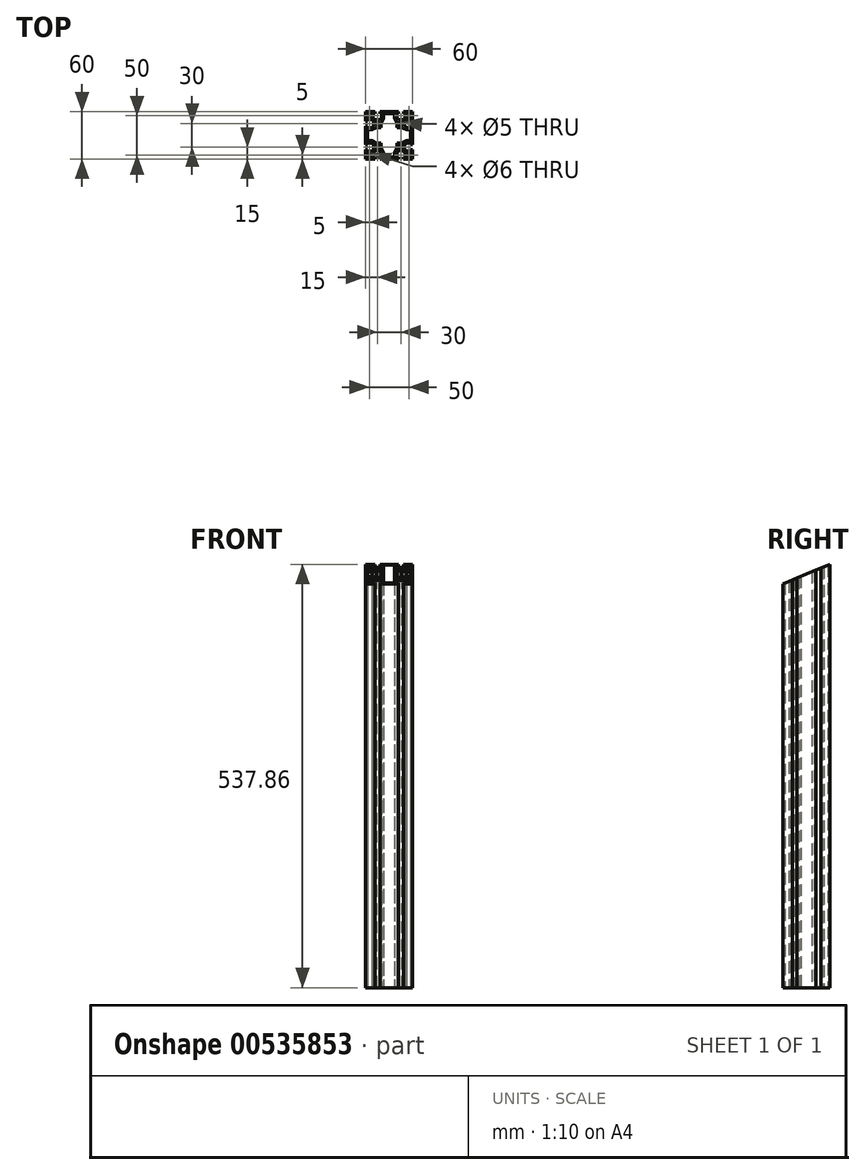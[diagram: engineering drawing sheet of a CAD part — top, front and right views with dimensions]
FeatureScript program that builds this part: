
annotation { "Feature Type Name" : "Feature", "Feature Type Description" : "" }
export const myFeature = defineFeature(function(context is Context, id is Id, definition is map)
    precondition{}
    {
        {
            var Q0;
            Q0=qCreatedBy(makeId("Top.planeOp"),FACE);
            var sketch = newSketch(context, id + "F0", { "sketchPlane" : qUnion([Q0])});
            skLineSegment(sketch, "E0.bottom", {"start": v(30, -30) * mm, "end": v(-30, -30) * mm});
            skLineSegment(sketch, "E0.top", {"start": v(30, 30) * mm, "end": v(-30, 30) * mm});
            skLineSegment(sketch, "E0.left", {"start": v(30, -30) * mm, "end": v(30, 30) * mm});
            skLineSegment(sketch, "E0.right", {"start": v(-30, -30) * mm, "end": v(-30, 30) * mm});
            skPoint(sketch, "E0.middle", {"position": v(0, 0) * mm});
            skLineSegment(sketch, "E1.top", {"start": v(-11.85, 30) * mm, "end": v(-18.15, 30) * mm});
            skLineSegment(sketch, "E1.left", {"start": v(-11.85, 27.5) * mm, "end": v(-11.85, 30) * mm});
            skLineSegment(sketch, "E1.right", {"start": v(-18.15, 27.5) * mm, "end": v(-18.15, 30) * mm});
            skPoint(sketch, "E1.middle", {"position": v(-15, 28.75) * mm});
            skLineSegment(sketch, "E2.bottom", {"start": v(-9.85, 27.5) * mm, "end": v(-11.85, 27.5) * mm});
            skLineSegment(sketch, "E2.left", {"start": v(-9.85, 27.5) * mm, "end": v(-9.85, 21.55) * mm});
            skLineSegment(sketch, "E2.right", {"start": v(-20.15, 27.5) * mm, "end": v(-20.15, 21.55) * mm});
            skPoint(sketch, "E2.middle", {"position": v(-15, 24.52) * mm});
            skArc(sketch, "E3", {"start": v(-20.15, 21.55) * mm, "mid": v(-15, 19.5) * mm, "end": v(-9.85, 21.55) * mm});
            skPoint(sketch, "E4.MirrorP", {"position": v(15, 24.52) * mm});
            skPoint(sketch, "E5.MirrorP", {"position": v(15, 28.75) * mm});
            skLineSegment(sketch, "E6.MirrorCS", {"start": v(11.85, 27.5) * mm, "end": v(11.85, 30) * mm});
            skLineSegment(sketch, "E7.MirrorCS", {"start": v(18.15, 27.5) * mm, "end": v(18.15, 30) * mm});
            skLineSegment(sketch, "E8.MirrorCS", {"start": v(9.85, 27.5) * mm, "end": v(11.85, 27.5) * mm});
            skLineSegment(sketch, "E9.MirrorCS", {"start": v(9.85, 27.5) * mm, "end": v(9.85, 21.55) * mm});
            skArc(sketch, "E10.MirrorCS", {"start": v(20.15, 21.55) * mm, "mid": v(15, 19.5) * mm, "end": v(9.85, 21.55) * mm});
            skLineSegment(sketch, "E11.MirrorCS", {"start": v(20.15, 27.5) * mm, "end": v(20.15, 21.55) * mm});
            skLineSegment(sketch, "E12.MirrorCS", {"start": v(11.85, 30) * mm, "end": v(18.15, 30) * mm});
            skLineSegment(sketch, "E13.1.0", {"start": v(27.5, 20.15) * mm, "end": v(21.55, 20.15) * mm});
            skLineSegment(sketch, "E13.1.1", {"start": v(27.5, 9.85) * mm, "end": v(21.55, 9.85) * mm});
            skArc(sketch, "E13.1.2", {"start": v(21.55, 20.15) * mm, "mid": v(19.5, 15) * mm, "end": v(21.55, 9.85) * mm});
            skLineSegment(sketch, "E13.1.3", {"start": v(27.5, -9.85) * mm, "end": v(21.55, -9.85) * mm});
            skLineSegment(sketch, "E13.1.4", {"start": v(27.5, -20.15) * mm, "end": v(21.55, -20.15) * mm});
            skPoint(sketch, "E13.1.5", {"position": v(28.75, 15) * mm});
            skPoint(sketch, "E13.1.6", {"position": v(28.75, -15) * mm});
            skArc(sketch, "E13.1.7", {"start": v(21.55, -20.15) * mm, "mid": v(19.5, -15) * mm, "end": v(21.55, -9.85) * mm});
            skPoint(sketch, "E13.1.8", {"position": v(24.52, -15) * mm});
            skPoint(sketch, "E13.1.9", {"position": v(24.52, 15) * mm});
            skLineSegment(sketch, "E13.1.10", {"start": v(27.5, 9.85) * mm, "end": v(27.5, 20.15) * mm});
            skLineSegment(sketch, "E13.1.11", {"start": v(27.5, -11.85) * mm, "end": v(27.5, -18.15) * mm});
            skLineSegment(sketch, "E13.1.12", {"start": v(30, 11.85) * mm, "end": v(30, 18.15) * mm});
            skLineSegment(sketch, "E13.1.13", {"start": v(30, -11.85) * mm, "end": v(30, -18.15) * mm});
            skLineSegment(sketch, "E13.1.14", {"start": v(27.5, 18.15) * mm, "end": v(30, 18.15) * mm});
            skLineSegment(sketch, "E13.1.15", {"start": v(27.5, 11.85) * mm, "end": v(30, 11.85) * mm});
            skLineSegment(sketch, "E13.1.16", {"start": v(27.5, 11.85) * mm, "end": v(27.5, 18.15) * mm});
            skLineSegment(sketch, "E13.1.17", {"start": v(27.5, -9.85) * mm, "end": v(27.5, -20.15) * mm});
            skLineSegment(sketch, "E13.1.18", {"start": v(27.5, -18.15) * mm, "end": v(30, -18.15) * mm});
            skLineSegment(sketch, "E13.1.19", {"start": v(27.5, -11.85) * mm, "end": v(30, -11.85) * mm});
            skLineSegment(sketch, "E13.2.0", {"start": v(20.15, -27.5) * mm, "end": v(20.15, -21.55) * mm});
            skLineSegment(sketch, "E13.2.1", {"start": v(9.85, -27.5) * mm, "end": v(9.85, -21.55) * mm});
            skArc(sketch, "E13.2.2", {"start": v(20.15, -21.55) * mm, "mid": v(15, -19.5) * mm, "end": v(9.85, -21.55) * mm});
            skLineSegment(sketch, "E13.2.3", {"start": v(-9.85, -27.5) * mm, "end": v(-9.85, -21.55) * mm});
            skLineSegment(sketch, "E13.2.4", {"start": v(-20.15, -27.5) * mm, "end": v(-20.15, -21.55) * mm});
            skPoint(sketch, "E13.2.5", {"position": v(15, -28.75) * mm});
            skPoint(sketch, "E13.2.6", {"position": v(-15, -28.75) * mm});
            skArc(sketch, "E13.2.7", {"start": v(-20.15, -21.55) * mm, "mid": v(-15, -19.5) * mm, "end": v(-9.85, -21.55) * mm});
            skPoint(sketch, "E13.2.8", {"position": v(-15, -24.52) * mm});
            skPoint(sketch, "E13.2.9", {"position": v(15, -24.52) * mm});
            skLineSegment(sketch, "E13.2.10", {"start": v(9.85, -27.5) * mm, "end": v(20.15, -27.5) * mm});
            skLineSegment(sketch, "E13.2.11", {"start": v(-11.85, -27.5) * mm, "end": v(-18.15, -27.5) * mm});
            skLineSegment(sketch, "E13.2.12", {"start": v(11.85, -30) * mm, "end": v(18.15, -30) * mm});
            skLineSegment(sketch, "E13.2.13", {"start": v(-11.85, -30) * mm, "end": v(-18.15, -30) * mm});
            skLineSegment(sketch, "E13.2.14", {"start": v(18.15, -27.5) * mm, "end": v(18.15, -30) * mm});
            skLineSegment(sketch, "E13.2.15", {"start": v(11.85, -27.5) * mm, "end": v(11.85, -30) * mm});
            skLineSegment(sketch, "E13.2.16", {"start": v(11.85, -27.5) * mm, "end": v(18.15, -27.5) * mm});
            skLineSegment(sketch, "E13.2.17", {"start": v(-9.85, -27.5) * mm, "end": v(-20.15, -27.5) * mm});
            skLineSegment(sketch, "E13.2.18", {"start": v(-18.15, -27.5) * mm, "end": v(-18.15, -30) * mm});
            skLineSegment(sketch, "E13.2.19", {"start": v(-11.85, -27.5) * mm, "end": v(-11.85, -30) * mm});
            skLineSegment(sketch, "E13.3.0", {"start": v(-27.5, -20.15) * mm, "end": v(-21.55, -20.15) * mm});
            skLineSegment(sketch, "E13.3.1", {"start": v(-27.5, -9.85) * mm, "end": v(-21.55, -9.85) * mm});
            skArc(sketch, "E13.3.2", {"start": v(-21.55, -20.15) * mm, "mid": v(-19.5, -15) * mm, "end": v(-21.55, -9.85) * mm});
            skLineSegment(sketch, "E13.3.3", {"start": v(-27.5, 9.85) * mm, "end": v(-21.55, 9.85) * mm});
            skLineSegment(sketch, "E13.3.4", {"start": v(-27.5, 20.15) * mm, "end": v(-21.55, 20.15) * mm});
            skPoint(sketch, "E13.3.5", {"position": v(-28.75, -15) * mm});
            skPoint(sketch, "E13.3.6", {"position": v(-28.75, 15) * mm});
            skArc(sketch, "E13.3.7", {"start": v(-21.55, 20.15) * mm, "mid": v(-19.5, 15) * mm, "end": v(-21.55, 9.85) * mm});
            skPoint(sketch, "E13.3.8", {"position": v(-24.52, 15) * mm});
            skPoint(sketch, "E13.3.9", {"position": v(-24.52, -15) * mm});
            skLineSegment(sketch, "E13.3.10", {"start": v(-27.5, -9.85) * mm, "end": v(-27.5, -20.15) * mm});
            skLineSegment(sketch, "E13.3.11", {"start": v(-27.5, 11.85) * mm, "end": v(-27.5, 18.15) * mm});
            skLineSegment(sketch, "E13.3.12", {"start": v(-30, -11.85) * mm, "end": v(-30, -18.15) * mm});
            skLineSegment(sketch, "E13.3.13", {"start": v(-30, 11.85) * mm, "end": v(-30, 18.15) * mm});
            skLineSegment(sketch, "E13.3.14", {"start": v(-27.5, -18.15) * mm, "end": v(-30, -18.15) * mm});
            skLineSegment(sketch, "E13.3.15", {"start": v(-27.5, -11.85) * mm, "end": v(-30, -11.85) * mm});
            skLineSegment(sketch, "E13.3.16", {"start": v(-27.5, -11.85) * mm, "end": v(-27.5, -18.15) * mm});
            skLineSegment(sketch, "E13.3.17", {"start": v(-27.5, 9.85) * mm, "end": v(-27.5, 20.15) * mm});
            skLineSegment(sketch, "E13.3.18", {"start": v(-27.5, 18.15) * mm, "end": v(-30, 18.15) * mm});
            skLineSegment(sketch, "E13.3.19", {"start": v(-27.5, 11.85) * mm, "end": v(-30, 11.85) * mm});
            skLineSegment(sketch, "E13.anchor1", {"start": v(0, 0) * mm, "end": v(-20.15, 21.55) * mm, "construction": true});
            skLineSegment(sketch, "E13.anchor2", {"start": v(0, 0) * mm, "end": v(-21.55, -20.15) * mm, "construction": true});
            skLineSegment(sketch, "E14.trimOffspring", {"start": v(-18.15, 27.5) * mm, "end": v(-20.15, 27.5) * mm});
            skLineSegment(sketch, "E15.trimOffspring", {"start": v(18.15, 27.5) * mm, "end": v(20.15, 27.5) * mm});
            skCircle(sketch, "E16", {"center": v(-15, 15) * mm, "radius": 2.5 * mm});
            skCircle(sketch, "E17", {"center": v(-25, 25) * mm, "radius": 3 * mm});
            skCircle(sketch, "E18.MirrorC", {"center": v(25, 25) * mm, "radius": 3 * mm});
            skCircle(sketch, "E19.MirrorC", {"center": v(25, -25) * mm, "radius": 3 * mm});
            skCircle(sketch, "E20.MirrorC", {"center": v(-25, -25) * mm, "radius": 3 * mm});
            skCircle(sketch, "E21.MirrorC", {"center": v(15, 15) * mm, "radius": 2.5 * mm});
            skCircle(sketch, "E22.MirrorC", {"center": v(15, -15) * mm, "radius": 2.5 * mm});
            skCircle(sketch, "E23.MirrorC", {"center": v(-15, -15) * mm, "radius": 2.5 * mm});
            skLineSegment(sketch, "E24", {"start": v(-7, 27.5) * mm, "end": v(0, 27.5) * mm});
            skLineSegment(sketch, "E25", {"start": v(-7, 27.5) * mm, "end": v(-7, 22) * mm});
            skLineSegment(sketch, "E26", {"start": v(-10, 10) * mm, "end": v(-10, 16) * mm});
            skLineSegment(sketch, "E27", {"start": v(-10, 16) * mm, "end": v(-7, 22) * mm});
            skLineSegment(sketch, "E28.MirrorCS", {"start": v(10, 10) * mm, "end": v(10, 16) * mm});
            skLineSegment(sketch, "E29.MirrorCS", {"start": v(10, 16) * mm, "end": v(7, 22) * mm});
            skLineSegment(sketch, "E30.MirrorCS", {"start": v(7, 27.5) * mm, "end": v(0, 27.5) * mm});
            skLineSegment(sketch, "E31.MirrorCS", {"start": v(7, 27.5) * mm, "end": v(7, 22) * mm});
            skLineSegment(sketch, "E32.1.0", {"start": v(-10, -10) * mm, "end": v(-16, -10) * mm});
            skLineSegment(sketch, "E32.1.1", {"start": v(-16, -10) * mm, "end": v(-22, -7) * mm});
            skLineSegment(sketch, "E32.1.2", {"start": v(-27.5, -7) * mm, "end": v(-22, -7) * mm});
            skLineSegment(sketch, "E32.1.3", {"start": v(-27.5, -7) * mm, "end": v(-27.5, 0) * mm});
            skLineSegment(sketch, "E32.1.4", {"start": v(-27.5, 7) * mm, "end": v(-27.5, 0) * mm});
            skLineSegment(sketch, "E32.1.5", {"start": v(-27.5, 7) * mm, "end": v(-22, 7) * mm});
            skLineSegment(sketch, "E32.1.6", {"start": v(-16, 10) * mm, "end": v(-22, 7) * mm});
            skLineSegment(sketch, "E32.1.7", {"start": v(-10, 10) * mm, "end": v(-16, 10) * mm});
            skLineSegment(sketch, "E32.2.0", {"start": v(10, -10) * mm, "end": v(10, -16) * mm});
            skLineSegment(sketch, "E32.2.1", {"start": v(10, -16) * mm, "end": v(7, -22) * mm});
            skLineSegment(sketch, "E32.2.2", {"start": v(7, -27.5) * mm, "end": v(7, -22) * mm});
            skLineSegment(sketch, "E32.2.3", {"start": v(7, -27.5) * mm, "end": v(0, -27.5) * mm});
            skLineSegment(sketch, "E32.2.4", {"start": v(-7, -27.5) * mm, "end": v(0, -27.5) * mm});
            skLineSegment(sketch, "E32.2.5", {"start": v(-7, -27.5) * mm, "end": v(-7, -22) * mm});
            skLineSegment(sketch, "E32.2.6", {"start": v(-10, -16) * mm, "end": v(-7, -22) * mm});
            skLineSegment(sketch, "E32.2.7", {"start": v(-10, -10) * mm, "end": v(-10, -16) * mm});
            skLineSegment(sketch, "E32.3.0", {"start": v(10, 10) * mm, "end": v(16, 10) * mm});
            skLineSegment(sketch, "E32.3.1", {"start": v(16, 10) * mm, "end": v(22, 7) * mm});
            skLineSegment(sketch, "E32.3.2", {"start": v(27.5, 7) * mm, "end": v(22, 7) * mm});
            skLineSegment(sketch, "E32.3.3", {"start": v(27.5, 7) * mm, "end": v(27.5, 0) * mm});
            skLineSegment(sketch, "E32.3.4", {"start": v(27.5, -7) * mm, "end": v(27.5, 0) * mm});
            skLineSegment(sketch, "E32.3.5", {"start": v(27.5, -7) * mm, "end": v(22, -7) * mm});
            skLineSegment(sketch, "E32.3.6", {"start": v(16, -10) * mm, "end": v(22, -7) * mm});
            skLineSegment(sketch, "E32.3.7", {"start": v(10, -10) * mm, "end": v(16, -10) * mm});
            skSolve(sketch);
        }
        {
            var Q0;
            {var subQ30=sQuery(id+"F0.wireOp",EDGE,"E1.left");Q0=makeQuery(id+"F0.imprint","IMPRINT",FACE,{"disambiguationData":[TD([[makeQuery(id+"F0.imprint","IMPRINT",EDGE,{"derivedFrom":subQ30}),-1.0]])]});}
            extrude(context, id + "F1", {"entities" : qUnion([Q0]), "depth" : 537.86 * mm, "offsetDistance" : 25 * mm});
        }
        {
            var Q0;
            Q0=makeQuery(id+"F1.opExtrude","SWEPT_EDGE",EDGE,{"disambiguationData":[OSD([sQuery(id+"F0.wireOp",EDGE,"E24"),sQuery(id+"F0.wireOp",EDGE,"E25")])]});
            var Q1;
            Q1=makeQuery(id+"F1.opExtrude","SWEPT_EDGE",EDGE,{"disambiguationData":[OSD([sQuery(id+"F0.wireOp",EDGE,"E30.MirrorCS"),sQuery(id+"F0.wireOp",EDGE,"E31.MirrorCS")])]});
            var Q2;
            Q2=makeQuery(id+"F1.opExtrude","SWEPT_EDGE",EDGE,{"disambiguationData":[OSD([sQuery(id+"F0.wireOp",EDGE,"840db5bc-c403-45cd-90c7-254e62d9e8c5.3.2"),sQuery(id+"F0.wireOp",EDGE,"840db5bc-c403-45cd-90c7-254e62d9e8c5.3.3")])]});
            var Q3;
            Q3=makeQuery(id+"F1.opExtrude","SWEPT_EDGE",EDGE,{"disambiguationData":[OSD([sQuery(id+"F0.wireOp",EDGE,"840db5bc-c403-45cd-90c7-254e62d9e8c5.3.4"),sQuery(id+"F0.wireOp",EDGE,"840db5bc-c403-45cd-90c7-254e62d9e8c5.3.5")])]});
            var Q4;
            Q4=makeQuery(id+"F1.opExtrude","SWEPT_EDGE",EDGE,{"disambiguationData":[OSD([sQuery(id+"F0.wireOp",EDGE,"840db5bc-c403-45cd-90c7-254e62d9e8c5.1.4"),sQuery(id+"F0.wireOp",EDGE,"840db5bc-c403-45cd-90c7-254e62d9e8c5.1.5")])]});
            var Q5;
            Q5=makeQuery(id+"F1.opExtrude","SWEPT_EDGE",EDGE,{"disambiguationData":[OSD([sQuery(id+"F0.wireOp",EDGE,"840db5bc-c403-45cd-90c7-254e62d9e8c5.1.2"),sQuery(id+"F0.wireOp",EDGE,"840db5bc-c403-45cd-90c7-254e62d9e8c5.1.3")])]});
            var Q6;
            Q6=makeQuery(id+"F1.opExtrude","SWEPT_EDGE",EDGE,{"disambiguationData":[OSD([sQuery(id+"F0.wireOp",EDGE,"840db5bc-c403-45cd-90c7-254e62d9e8c5.2.2"),sQuery(id+"F0.wireOp",EDGE,"840db5bc-c403-45cd-90c7-254e62d9e8c5.2.3")])]});
            var Q7;
            Q7=makeQuery(id+"F1.opExtrude","SWEPT_EDGE",EDGE,{"disambiguationData":[OSD([sQuery(id+"F0.wireOp",EDGE,"840db5bc-c403-45cd-90c7-254e62d9e8c5.2.4"),sQuery(id+"F0.wireOp",EDGE,"840db5bc-c403-45cd-90c7-254e62d9e8c5.2.5")])]});
            fillet(context, id + "F2", {"entities" : qUnion([Q0, Q1, Q2, Q3, Q4, Q5, Q6, Q7]), "radius" : 2 * mm, "tangentPropagation" : true, "allowEdgeOverflow" : false});
        }
        {
            var Q0;
            Q0=makeQuery(id+"F1.opExtrude","SWEPT_EDGE",EDGE,{"disambiguationData":[OSD([sQuery(id+"F0.wireOp",EDGE,"E26"),sQuery(id+"F0.wireOp",EDGE,"E27")])]});
            var Q1;
            Q1=makeQuery(id+"F1.opExtrude","SWEPT_EDGE",EDGE,{"disambiguationData":[OSD([sQuery(id+"F0.wireOp",EDGE,"E28.MirrorCS"),sQuery(id+"F0.wireOp",EDGE,"E29.MirrorCS")])]});
            var Q2;
            Q2=makeQuery(id+"F1.opExtrude","SWEPT_EDGE",EDGE,{"disambiguationData":[OSD([sQuery(id+"F0.wireOp",EDGE,"840db5bc-c403-45cd-90c7-254e62d9e8c5.3.0"),sQuery(id+"F0.wireOp",EDGE,"840db5bc-c403-45cd-90c7-254e62d9e8c5.3.1")])]});
            var Q3;
            Q3=makeQuery(id+"F1.opExtrude","SWEPT_EDGE",EDGE,{"disambiguationData":[OSD([sQuery(id+"F0.wireOp",EDGE,"840db5bc-c403-45cd-90c7-254e62d9e8c5.1.6"),sQuery(id+"F0.wireOp",EDGE,"840db5bc-c403-45cd-90c7-254e62d9e8c5.1.7")])]});
            var Q4;
            Q4=makeQuery(id+"F1.opExtrude","SWEPT_EDGE",EDGE,{"disambiguationData":[OSD([sQuery(id+"F0.wireOp",EDGE,"840db5bc-c403-45cd-90c7-254e62d9e8c5.1.0"),sQuery(id+"F0.wireOp",EDGE,"840db5bc-c403-45cd-90c7-254e62d9e8c5.1.1")])]});
            var Q5;
            Q5=makeQuery(id+"F1.opExtrude","SWEPT_EDGE",EDGE,{"disambiguationData":[OSD([sQuery(id+"F0.wireOp",EDGE,"840db5bc-c403-45cd-90c7-254e62d9e8c5.3.6"),sQuery(id+"F0.wireOp",EDGE,"840db5bc-c403-45cd-90c7-254e62d9e8c5.3.7")])]});
            var Q6;
            Q6=makeQuery(id+"F1.opExtrude","SWEPT_EDGE",EDGE,{"disambiguationData":[OSD([sQuery(id+"F0.wireOp",EDGE,"840db5bc-c403-45cd-90c7-254e62d9e8c5.2.0"),sQuery(id+"F0.wireOp",EDGE,"840db5bc-c403-45cd-90c7-254e62d9e8c5.2.1")])]});
            var Q7;
            Q7=makeQuery(id+"F1.opExtrude","SWEPT_EDGE",EDGE,{"disambiguationData":[OSD([sQuery(id+"F0.wireOp",EDGE,"840db5bc-c403-45cd-90c7-254e62d9e8c5.2.6"),sQuery(id+"F0.wireOp",EDGE,"840db5bc-c403-45cd-90c7-254e62d9e8c5.2.7")])]});
            fillet(context, id + "F3", {"entities" : qUnion([Q0, Q1, Q2, Q3, Q4, Q5, Q6, Q7]), "radius" : 7 * mm, "tangentPropagation" : true, "allowEdgeOverflow" : false});
        }
        {
            var Q0;
            Q0=qCreatedBy(makeId("Right.planeOp"),FACE);
            var sketch = newSketch(context, id + "F4", { "sketchPlane" : qUnion([Q0])});
            skLineSegment(sketch, "E33.bottom", {"start": v(-234.13, 733.04) * mm, "end": v(-77.69, 797.84) * mm});
            skLineSegment(sketch, "E33.top", {"start": v(-126.44, 473.06) * mm, "end": v(30, 537.86) * mm});
            skLineSegment(sketch, "E33.left", {"start": v(-234.13, 733.04) * mm, "end": v(-126.44, 473.06) * mm});
            skLineSegment(sketch, "E33.right", {"start": v(-77.69, 797.84) * mm, "end": v(30, 537.86) * mm});
            skSolve(sketch);
        }
        {
            var Q0;
            Q0=makeQuery(id+"F4.imprint","IMPRINT",FACE,{"disambiguationData":[TD([[makeQuery(id+"F4.imprint","IMPRINT",EDGE,{"derivedFrom":sQuery(id+"F4.wireOp",EDGE,"E33.bottom")}),-1.0]])]});
            extrude(context, id + "F5", {"entities" : qUnion([Q0]), "operationType" : NewBodyOperationType.REMOVE, "depth" : 30 * mm, "offsetDistance" : 25 * mm, "hasSecondDirection" : true, "secondDirectionOppositeDirection" : true, "secondDirectionDepth" : 30 * mm});
        }
    });
